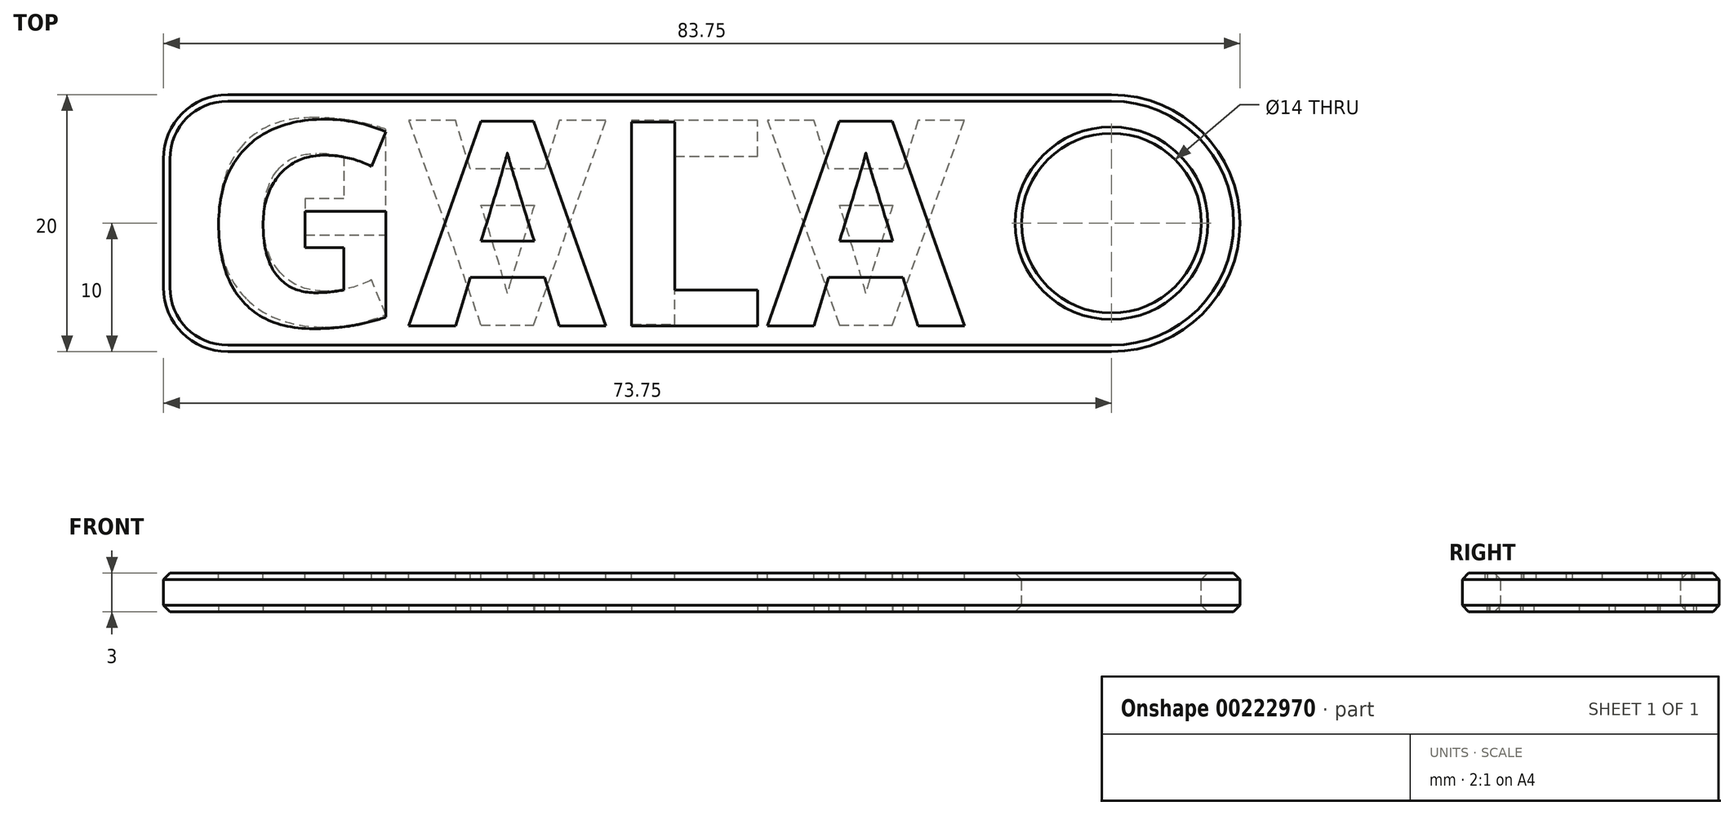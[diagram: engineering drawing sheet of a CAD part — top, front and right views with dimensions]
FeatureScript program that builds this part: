
annotation { "Feature Type Name" : "Feature", "Feature Type Description" : "" }
export const myFeature = defineFeature(function(context is Context, id is Id, definition is map)
    precondition{}
    {
        {
            var Q0;
            Q0=qCreatedBy(makeId("Top.planeOp"),FACE);
            var sketch = newSketch(context, id + "F0", { "sketchPlane" : qUnion([Q0])});
            skCircle(sketch, "E0", {"center": v(0, 0) * mm, "radius": 7 * mm});
            skArc(sketch, "E1", {"start": v(0, -10) * mm, "mid": v(10, 0) * mm, "end": v(0, 10) * mm});
            skLineSegment(sketch, "E2", {"start": v(0, 10) * mm, "end": v(-68.75, 10) * mm});
            skLineSegment(sketch, "E3", {"start": v(-73.75, 5) * mm, "end": v(-73.75, -5) * mm});
            skLineSegment(sketch, "E4", {"start": v(-68.75, -10) * mm, "end": v(0, -10) * mm});
            skText(sketch, "E5", { "text": "GALA", "fontName": "OpenSans-Bold.ttf"});
            skLineSegment(sketch, "E6", {"start": v(-10, 0) * mm, "end": v(-7, 0) * mm, "construction": true});
            skLineSegment(sketch, "E7", {"start": v(-70.75, 0) * mm, "end": v(-73.75, 0) * mm, "construction": true});
            skLineSegment(sketch, "E8", {"start": v(-40.38, 8) * mm, "end": v(-40.38, 10) * mm, "construction": true});
            skLineSegment(sketch, "E9", {"start": v(-40.38, -8) * mm, "end": v(-40.38, -10) * mm, "construction": true});
            skPoint(sketch, "E10.visualSharp", {"position": v(-73.75, 10) * mm});
            skArc(sketch, "E10.filletArc", {"start": v(-68.75, 10) * mm, "mid": v(-72.29, 8.54) * mm, "end": v(-73.75, 5) * mm});
            skPoint(sketch, "E11.visualSharp", {"position": v(-73.75, -10) * mm});
            skArc(sketch, "E11.filletArc", {"start": v(-73.75, -5) * mm, "mid": v(-72.29, -8.54) * mm, "end": v(-68.75, -10) * mm});
            const initialGuessF0  = {"E5": [-0.07075, -0.008, 1, 0, 0.016]};
            skSetInitialGuess(sketch, initialGuessF0);
            skSolve(sketch);
        }
        {
            var Q0;
            Q0=makeQuery(id+"F0.imprint","IMPRINT",FACE,{"disambiguationData":[TD([[makeQuery(id+"F0.imprint","IMPRINT",EDGE,{"derivedFrom":sQuery(id+"F0.wireOp",EDGE,"E0")}),-1.0]])]});
            var Q1;
            Q1=makeQuery(id+"F0.imprint","IMPRINT",FACE,{"disambiguationData":[TD([[makeQuery(id+"F0.imprint","IMPRINT",EDGE,{"derivedFrom":sQuery(id+"F0.wireOp",EDGE,"E5.sketch_text.stroke-37")}),-1.0]])]});
            var Q2;
            Q2=makeQuery(id+"F0.imprint","IMPRINT",FACE,{"disambiguationData":[TD([[makeQuery(id+"F0.imprint","IMPRINT",EDGE,{"derivedFrom":sQuery(id+"F0.wireOp",EDGE,"E5.sketch_text.stroke-45")}),1.0]])]});
            var Q3;
            Q3=makeQuery(id+"F0.imprint","IMPRINT",FACE,{"disambiguationData":[TD([[makeQuery(id+"F0.imprint","IMPRINT",EDGE,{"derivedFrom":sQuery(id+"F0.wireOp",EDGE,"E5.sketch_text.stroke-31")}),-1.0]])]});
            var Q4;
            Q4=makeQuery(id+"F0.imprint","IMPRINT",FACE,{"disambiguationData":[TD([[makeQuery(id+"F0.imprint","IMPRINT",EDGE,{"derivedFrom":sQuery(id+"F0.wireOp",EDGE,"E5.sketch_text.stroke-19")}),-1.0]])]});
            var Q5;
            Q5=makeQuery(id+"F0.imprint","IMPRINT",FACE,{"disambiguationData":[TD([[makeQuery(id+"F0.imprint","IMPRINT",EDGE,{"derivedFrom":sQuery(id+"F0.wireOp",EDGE,"E5.sketch_text.stroke-27")}),1.0]])]});
            var Q6;
            Q6=makeQuery(id+"F0.imprint","IMPRINT",FACE,{"disambiguationData":[TD([[makeQuery(id+"F0.imprint","IMPRINT",EDGE,{"derivedFrom":sQuery(id+"F0.wireOp",EDGE,"E5.sketch_text.stroke-0")}),-1.0]])]});
            extrude(context, id + "F1", {"entities" : qUnion([Q0, Q1, Q2, Q3, Q4, Q5, Q6]), "depth" : 3 * mm});
        }
        {
            var Q0;
            Q0=makeQuery(id+"F1.opExtrude","CAP_FACE",FACE,{"disambiguationData":[OSD([sQuery(id+"F0.wireOp",EDGE,"E0"),sQuery(id+"F0.wireOp",EDGE,"E1"),sQuery(id+"F0.wireOp",EDGE,"E2"),sQuery(id+"F0.wireOp",EDGE,"E3"),sQuery(id+"F0.wireOp",EDGE,"E4"),sQuery(id+"F0.wireOp",EDGE,"E10.filletArc"),sQuery(id+"F0.wireOp",EDGE,"E11.filletArc")])],"isStart":false});
            var sketch = newSketch(context, id + "F2", { "sketchPlane" : qUnion([Q0])});
            skPoint(sketch, "E12.0", {"position": v(-70.75, 8) * mm});
            skPoint(sketch, "E12.1", {"position": v(-10, -8) * mm});
            skText(sketch, "E13", { "text": "GALA", "fontName": "OpenSans-Bold.ttf"});
            const initialGuessF2  = {"E13": [-0.07075, -0.008, 1, 0, 0.016]};
            skSetInitialGuess(sketch, initialGuessF2);
            skSolve(sketch);
        }
        {
            var Q0;
            Q0 = qSketchRegion(id + "F2", true);
            extrude(context, id + "F3", {"entities" : qUnion([Q0]), "operationType" : NewBodyOperationType.REMOVE, "oppositeDirection" : true, "depth" : 0.5 * mm});
        }
        {
            var Q0;
            Q0=makeQuery(id+"F1.opExtrude","SWEPT_BODY",BODY,{"disambiguationData":[OSD([sQuery(id+"F0.wireOp",EDGE,"E0"),sQuery(id+"F0.wireOp",EDGE,"E1"),sQuery(id+"F0.wireOp",EDGE,"E2"),sQuery(id+"F0.wireOp",EDGE,"E3"),sQuery(id+"F0.wireOp",EDGE,"E4"),sQuery(id+"F0.wireOp",EDGE,"E10.filletArc"),sQuery(id+"F0.wireOp",EDGE,"E11.filletArc")])]});
            var Q1;
            Q1=sQuery(id+"F0.wireOp",EDGE,"E6");
            transform(context, id + "F4", {"entities" : qUnion([Q0]), "transformType" : TransformType.ROTATION, "transformAxis" : qUnion([Q1]), "angle" : 180 * degree, "makeCopy" : false});
        }
        {
            var Q0;
            Q0=makeQuery(id+"F0.imprint","IMPRINT",FACE,{"disambiguationData":[TD([[makeQuery(id+"F0.imprint","IMPRINT",EDGE,{"derivedFrom":sQuery(id+"F0.wireOp",EDGE,"E5.sketch_text.stroke-0")}),-1.0]])]});
            var Q1;
            Q1=makeQuery(id+"F0.imprint","IMPRINT",FACE,{"disambiguationData":[TD([[makeQuery(id+"F0.imprint","IMPRINT",EDGE,{"derivedFrom":sQuery(id+"F0.wireOp",EDGE,"E5.sketch_text.stroke-19")}),-1.0]])]});
            var Q2;
            Q2=makeQuery(id+"F0.imprint","IMPRINT",FACE,{"disambiguationData":[TD([[makeQuery(id+"F0.imprint","IMPRINT",EDGE,{"derivedFrom":sQuery(id+"F0.wireOp",EDGE,"E5.sketch_text.stroke-31")}),-1.0]])]});
            var Q3;
            Q3=makeQuery(id+"F0.imprint","IMPRINT",FACE,{"disambiguationData":[TD([[makeQuery(id+"F0.imprint","IMPRINT",EDGE,{"derivedFrom":sQuery(id+"F0.wireOp",EDGE,"E5.sketch_text.stroke-37")}),-1.0]])]});
            extrude(context, id + "F5", {"entities" : qUnion([Q0, Q1, Q2, Q3]), "operationType" : NewBodyOperationType.REMOVE, "oppositeDirection" : true, "depth" : 0.5 * mm});
        }
        {
            var Q0;
            Q0=makeQuery(id+"F1.opExtrude","CAP_EDGE",EDGE,{"disambiguationData":[OSD([sQuery(id+"F0.wireOp",EDGE,"E4")])],"isStart":true});
            var Q1;
            Q1=makeQuery(id+"F1.opExtrude","CAP_EDGE",EDGE,{"disambiguationData":[OSD([sQuery(id+"F0.wireOp",EDGE,"E0")])],"isStart":true});
            var Q2;
            Q2=makeQuery(id+"F1.opExtrude","CAP_EDGE",EDGE,{"disambiguationData":[OSD([sQuery(id+"F0.wireOp",EDGE,"E1")])],"isStart":false});
            var Q3;
            Q3=makeQuery(id+"F1.opExtrude","CAP_EDGE",EDGE,{"disambiguationData":[OSD([sQuery(id+"F0.wireOp",EDGE,"E0")])],"isStart":false});
            chamfer(context, id + "F6", {"entities" : qUnion([Q0, Q1, Q2, Q3]), "width" : 0.5 * mm, "tangentPropagation" : true});
        }
    });
